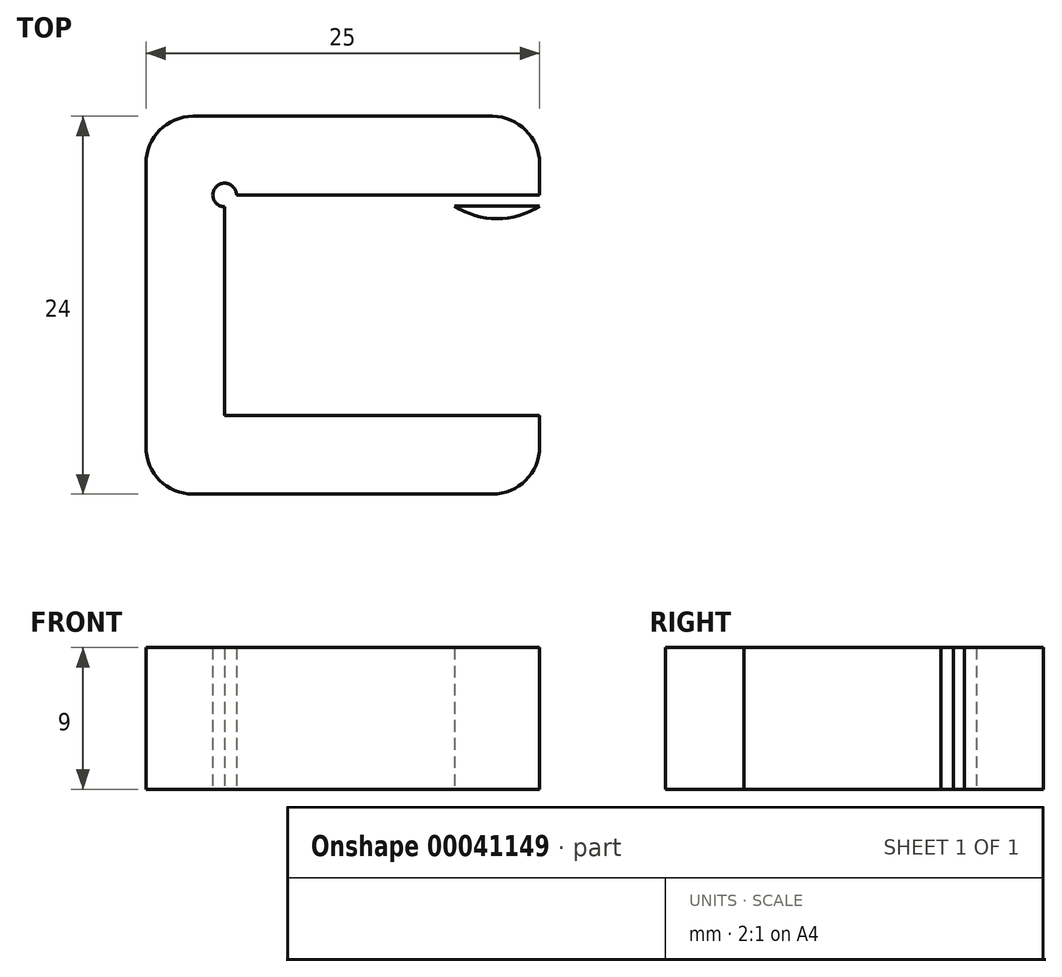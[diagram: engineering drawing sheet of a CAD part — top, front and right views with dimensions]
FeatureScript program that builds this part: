
annotation { "Feature Type Name" : "Feature", "Feature Type Description" : "" }
export const myFeature = defineFeature(function(context is Context, id is Id, definition is map)
    precondition{}
    {
        {
            var Q0;
            Q0=qCreatedBy(makeId("Top.planeOp"),FACE);
            var sketch = newSketch(context, id + "F0", { "sketchPlane" : qUnion([Q0])});
            skLineSegment(sketch, "E0.bottom", {"start": v(3.72, 11.24) * mm, "end": v(-21.28, 11.24) * mm});
            skLineSegment(sketch, "E0.top", {"start": v(3.72, -12.76) * mm, "end": v(-21.28, -12.76) * mm});
            skLineSegment(sketch, "E0.left", {"start": v(3.72, 11.24) * mm, "end": v(3.72, -12.76) * mm});
            skLineSegment(sketch, "E0.right", {"start": v(-21.28, 11.24) * mm, "end": v(-21.28, -12.76) * mm});
            skLineSegment(sketch, "E1.bottom", {"start": v(3.72, 6.24) * mm, "end": v(-16.28, 6.24) * mm});
            skLineSegment(sketch, "E1.top", {"start": v(3.72, -7.76) * mm, "end": v(-16.28, -7.76) * mm});
            skLineSegment(sketch, "E1.left", {"start": v(3.72, 6.24) * mm, "end": v(3.72, -7.76) * mm});
            skLineSegment(sketch, "E1.right", {"start": v(-16.28, 6.24) * mm, "end": v(-16.28, -7.76) * mm});
            skLineSegment(sketch, "E2.bottom", {"start": v(3.72, 6.24) * mm, "end": v(-1.66, 6.24) * mm});
            skLineSegment(sketch, "E2.top", {"start": v(3.72, 5.54) * mm, "end": v(-1.66, 5.54) * mm});
            skLineSegment(sketch, "E2.left", {"start": v(3.72, 6.24) * mm, "end": v(3.72, 5.54) * mm});
            skLineSegment(sketch, "E2.right", {"start": v(-1.66, 6.24) * mm, "end": v(-1.66, 5.54) * mm});
            skArc(sketch, "E3", {"start": v(-1.66, 5.54) * mm, "mid": v(1.03, 4.74) * mm, "end": v(3.72, 5.54) * mm});
            skCircle(sketch, "E4", {"center": v(-16.28, 6.24) * mm, "radius": 0.75 * mm});
            skSolve(sketch);
        }
        {
            var Q0;
            Q0=makeQuery(id+"F0.imprint","IMPRINT",FACE,{"disambiguationData":[TD([[makeQuery(id+"F0.imprint","IMPRINT",EDGE,{"derivedFrom":sQuery(id+"F0.wireOp",EDGE,"E2.top")}),1.0]])]});
            var Q1;
            Q1=makeQuery(id+"F0.imprint","IMPRINT",FACE,{"disambiguationData":[TD([[makeQuery(id+"F0.imprint","IMPRINT",EDGE,{"derivedFrom":sQuery(id+"F0.wireOp",EDGE,"E2.bottom")}),1.0]])]});
            var Q2;
            {var subQ6=sQuery(id+"F0.wireOp",EDGE,"E0.bottom");Q2=makeQuery(id+"F0.imprint","IMPRINT",FACE,{"disambiguationData":[TD([[makeQuery(id+"F0.imprint","IMPRINT",EDGE,{"derivedFrom":subQ6}),1.0]])]});}
            extrude(context, id + "F1", {"entities" : qUnion([Q0, Q1, Q2]), "depth" : 9 * mm});
        }
        {
            var Q0;
            Q0=makeQuery(id+"F1.opExtrude","SWEPT_EDGE",EDGE,{"disambiguationData":[OSD([sQuery(id+"F0.wireOp",EDGE,"E0.bottom"),sQuery(id+"F0.wireOp",EDGE,"E0.right")])]});
            var Q1;
            Q1=makeQuery(id+"F1.opExtrude","SWEPT_EDGE",EDGE,{"disambiguationData":[OSD([sQuery(id+"F0.wireOp",EDGE,"E0.top"),sQuery(id+"F0.wireOp",EDGE,"E0.right")])]});
            var Q2;
            Q2=makeQuery(id+"F1.opExtrude","SWEPT_EDGE",EDGE,{"disambiguationData":[OSD([sQuery(id+"F0.wireOp",EDGE,"E0.bottom"),sQuery(id+"F0.wireOp",EDGE,"E0.left")])]});
            var Q3;
            Q3=makeQuery(id+"F1.opExtrude","SWEPT_EDGE",EDGE,{"disambiguationData":[OSD([sQuery(id+"F0.wireOp",EDGE,"E0.top"),sQuery(id+"F0.wireOp",EDGE,"E0.left")])]});
            fillet(context, id + "F2", {"entities" : qUnion([Q0, Q1, Q2, Q3]), "radius" : 3 * mm, "tangentPropagation" : true, "allowEdgeOverflow" : false});
        }
    });
